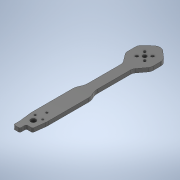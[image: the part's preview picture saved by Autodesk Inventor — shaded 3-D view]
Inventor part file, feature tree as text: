
AUTODESK INVENTOR PART (.ipt)
format: ipt  version: 2020 (Build 240168000, 168)  size: 265,728 bytes
history: native  units: in
note: dims shown in document units (in); Inventor stores cm internally (conversion verified against a paired STEP export)
features: sketch x3, extrude x2, fillet x2
ambient origin geometry x8: Origin, YZ Plane, XZ Plane, XY Plane, X Axis, Y Axis, Z Axis, Center Point
bodies: Body1 (feature_tree)
feature tree (7):
  extrude  "Extrusion1"  Depth=0.2362in
  sketch  "Sketch4"  dims[d7=0.4724in d9=7.0in d10=6.8898in d11=6.8898in]
  extrude  "Extrusion2"  Depth=7.0in
  fillet  "Fillet2"  Radius=6.8898in
  fillet  "Fillet3"  Radius=6.8898in
  sketch  "Sketch3"  dims[d2=0.2362in d3=0.0in d4=0.8352in]
  sketch  "Sketch5"  dims[d12=0.2992in d13=0.2992in d14=0.9835in d15=0.9835in d16=0.9835in d17=0.1181in d18=0.0in d20=0.3937in d21=0.7874in]
